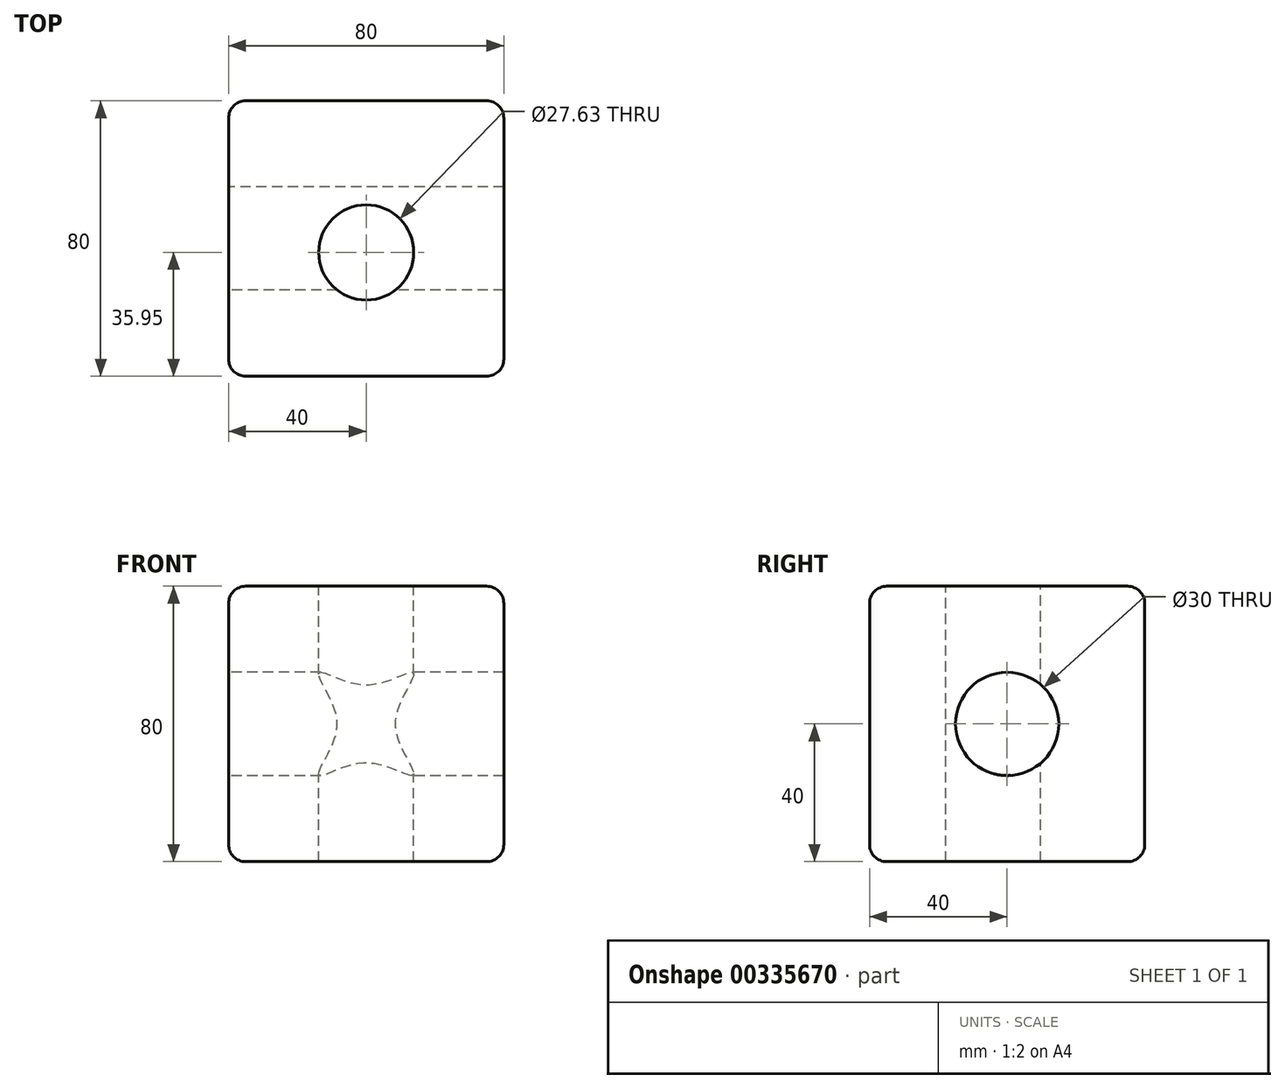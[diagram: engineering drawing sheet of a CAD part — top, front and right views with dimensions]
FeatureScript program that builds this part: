
annotation { "Feature Type Name" : "Feature", "Feature Type Description" : "" }
export const myFeature = defineFeature(function(context is Context, id is Id, definition is map)
    precondition{}
    {
        {
            var Q0;
            Q0=qCreatedBy(makeId("Top.planeOp"),FACE);
            var sketch = newSketch(context, id + "F0", { "sketchPlane" : qUnion([Q0])});
            skLineSegment(sketch, "E0.bottom", {"start": v(-40, 40) * mm, "end": v(40, 40) * mm});
            skLineSegment(sketch, "E0.top", {"start": v(-40, -40) * mm, "end": v(40, -40) * mm});
            skLineSegment(sketch, "E0.left", {"start": v(-40, 40) * mm, "end": v(-40, -40) * mm});
            skLineSegment(sketch, "E0.right", {"start": v(40, 40) * mm, "end": v(40, -40) * mm});
            skPoint(sketch, "E0.middle", {"position": v(0, 0) * mm});
            skSolve(sketch);
        }
        {
            var Q0;
            Q0=makeQuery(id+"F0.imprint","IMPRINT",FACE,{"disambiguationData":[TD([[makeQuery(id+"F0.imprint","IMPRINT",EDGE,{"derivedFrom":sQuery(id+"F0.wireOp",EDGE,"E0.bottom")}),-1.0]])]});
            extrude(context, id + "F1", {"entities" : qUnion([Q0]), "endBound" : BoundingType.SYMMETRIC, "depth" : 80 * mm});
        }
        {
            var Q0;
            Q0=makeQuery(id+"F1.opExtrude","CAP_EDGE",EDGE,{"disambiguationData":[OSD([sQuery(id+"F0.wireOp",EDGE,"E0.right")])],"isStart":false});
            var Q1;
            Q1=makeQuery(id+"F1.opExtrude","SWEPT_EDGE",EDGE,{"disambiguationData":[OSD([sQuery(id+"F0.wireOp",EDGE,"E0.top"),sQuery(id+"F0.wireOp",EDGE,"E0.right")])]});
            var Q2;
            Q2=makeQuery(id+"F1.opExtrude","SWEPT_FACE",FACE,{"disambiguationData":[OSD([sQuery(id+"F0.wireOp",EDGE,"E0.right")])]});
            var Q3;
            Q3=makeQuery(id+"F1.opExtrude","CAP_EDGE",EDGE,{"disambiguationData":[OSD([sQuery(id+"F0.wireOp",EDGE,"E0.top")])],"isStart":false});
            var Q4;
            Q4=makeQuery(id+"F1.opExtrude","SWEPT_FACE",FACE,{"disambiguationData":[OSD([sQuery(id+"F0.wireOp",EDGE,"E0.top")])]});
            var Q5;
            Q5=makeQuery(id+"F1.opExtrude","CAP_EDGE",EDGE,{"disambiguationData":[OSD([sQuery(id+"F0.wireOp",EDGE,"E0.top")])],"isStart":true});
            var Q6;
            Q6=makeQuery(id+"F1.opExtrude","CAP_EDGE",EDGE,{"disambiguationData":[OSD([sQuery(id+"F0.wireOp",EDGE,"E0.left")])],"isStart":false});
            var Q7;
            Q7=makeQuery(id+"F1.opExtrude","CAP_FACE",FACE,{"disambiguationData":[OSD([sQuery(id+"F0.wireOp",EDGE,"E0.bottom"),sQuery(id+"F0.wireOp",EDGE,"E0.top"),sQuery(id+"F0.wireOp",EDGE,"E0.left"),sQuery(id+"F0.wireOp",EDGE,"E0.right")])],"isStart":false});
            var Q8;
            Q8=makeQuery(id+"F1.opExtrude","CAP_EDGE",EDGE,{"disambiguationData":[OSD([sQuery(id+"F0.wireOp",EDGE,"E0.bottom")])],"isStart":false});
            var Q9;
            Q9=makeQuery(id+"F1.opExtrude","CAP_EDGE",EDGE,{"disambiguationData":[OSD([sQuery(id+"F0.wireOp",EDGE,"E0.left")])],"isStart":true});
            var Q10;
            Q10=makeQuery(id+"F1.opExtrude","CAP_EDGE",EDGE,{"disambiguationData":[OSD([sQuery(id+"F0.wireOp",EDGE,"E0.bottom")])],"isStart":true});
            var Q11;
            Q11=makeQuery(id+"F1.opExtrude","CAP_EDGE",EDGE,{"disambiguationData":[OSD([sQuery(id+"F0.wireOp",EDGE,"E0.right")])],"isStart":true});
            var Q12;
            Q12=makeQuery(id+"F1.opExtrude","SWEPT_EDGE",EDGE,{"disambiguationData":[OSD([sQuery(id+"F0.wireOp",EDGE,"E0.bottom"),sQuery(id+"F0.wireOp",EDGE,"E0.left")])]});
            fillet(context, id + "F2", {"entities" : qUnion([Q0, Q1, Q2, Q3, Q4, Q5, Q6, Q7, Q8, Q9, Q10, Q11, Q12]), "radius" : 5 * mm, "tangentPropagation" : true, "allowEdgeOverflow" : false});
        }
        {
            var Q0;
            Q0=makeQuery(id+"F1.opExtrude","CAP_FACE",FACE,{"disambiguationData":[OSD([sQuery(id+"F0.wireOp",EDGE,"E0.bottom"),sQuery(id+"F0.wireOp",EDGE,"E0.top"),sQuery(id+"F0.wireOp",EDGE,"E0.left"),sQuery(id+"F0.wireOp",EDGE,"E0.right")])],"isStart":false});
            var sketch = newSketch(context, id + "F3", { "sketchPlane" : qUnion([Q0])});
            skCircle(sketch, "E1", {"center": v(0, -4.05) * mm, "radius": 13.81 * mm});
            skSolve(sketch);
        }
        {
            var Q0;
            Q0=makeQuery(id+"F3.imprint","IMPRINT",FACE,{"disambiguationData":[TD([[makeQuery(id+"F3.imprint","IMPRINT",EDGE,{"derivedFrom":sQuery(id+"F3.wireOp",EDGE,"E1")}),1.0]])]});
            var Q1;
            Q1=sQuery(id+"F3.wireOp",EDGE,"E1");
            extrude(context, id + "F4", {"entities" : qUnion([Q0]), "operationType" : NewBodyOperationType.REMOVE, "surfaceEntities" : qUnion([Q1]), "endBound" : BoundingType.THROUGH_ALL, "oppositeDirection" : true, "depth" : 25 * mm});
        }
        {
            var Q0;
            Q0=makeQuery(id+"F1.opExtrude","SWEPT_FACE",FACE,{"disambiguationData":[OSD([sQuery(id+"F0.wireOp",EDGE,"E0.left")])]});
            var sketch = newSketch(context, id + "F5", { "sketchPlane" : qUnion([Q0])});
            skCircle(sketch, "E2", {"center": v(0, 0) * mm, "radius": 15 * mm});
            skSolve(sketch);
        }
        {
            var Q0;
            Q0=makeQuery(id+"F5.imprint","IMPRINT",FACE,{"disambiguationData":[TD([[makeQuery(id+"F5.imprint","IMPRINT",EDGE,{"derivedFrom":sQuery(id+"F5.wireOp",EDGE,"E2")}),1.0]])]});
            extrude(context, id + "F6", {"entities" : qUnion([Q0]), "operationType" : NewBodyOperationType.REMOVE, "endBound" : BoundingType.THROUGH_ALL, "oppositeDirection" : true, "depth" : 25 * mm});
        }
    });
